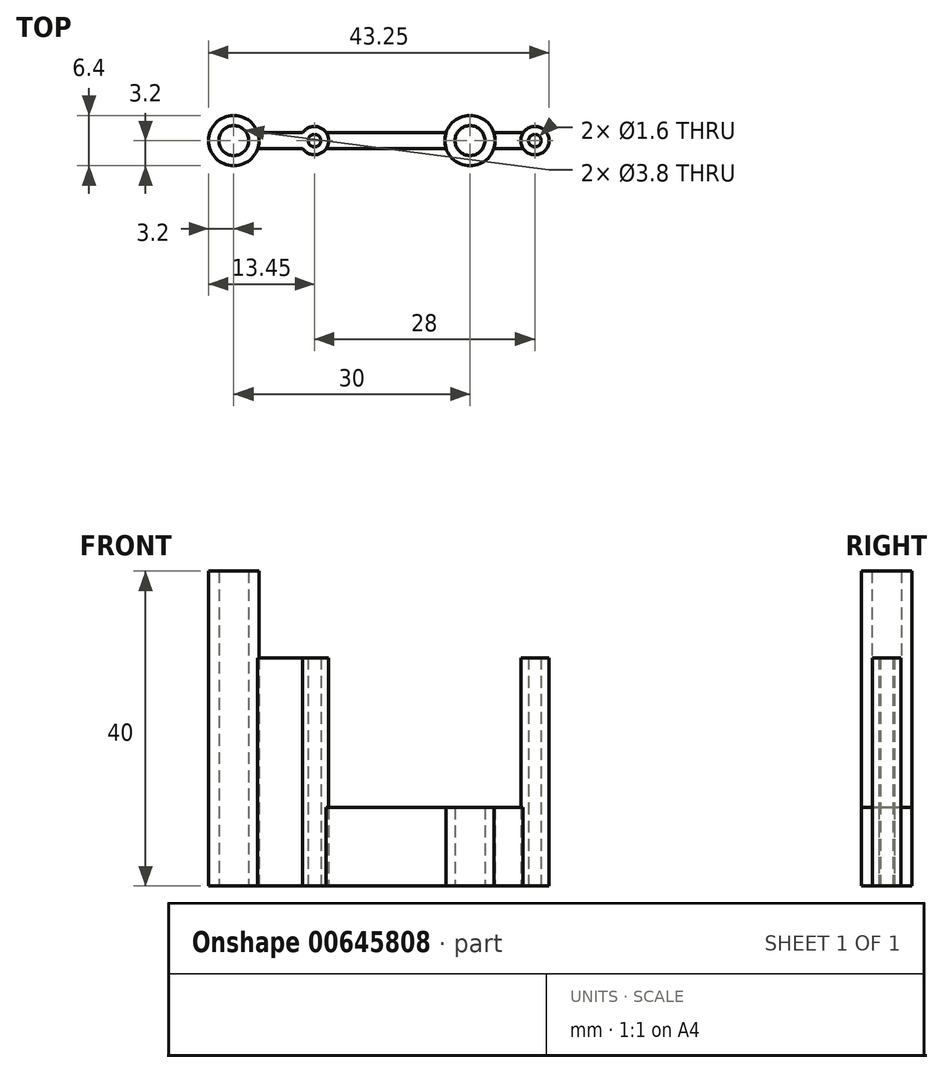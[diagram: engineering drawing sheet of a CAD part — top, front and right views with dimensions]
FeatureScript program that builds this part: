
annotation { "Feature Type Name" : "Feature", "Feature Type Description" : "" }
export const myFeature = defineFeature(function(context is Context, id is Id, definition is map)
    precondition{}
    {
        {
            var Q0;
            Q0=qCreatedBy(makeId("Top.planeOp"),FACE);
            var sketch = newSketch(context, id + "F0", { "sketchPlane" : qUnion([Q0])});
            skCircle(sketch, "E0", {"center": v(-30, 0) * mm, "radius": 3.2 * mm});
            skCircle(sketch, "E1", {"center": v(0, 0) * mm, "radius": 3.2 * mm});
            skCircle(sketch, "E2", {"center": v(-30, 0) * mm, "radius": 1.9 * mm});
            skCircle(sketch, "E3", {"center": v(0, 0) * mm, "radius": 1.9 * mm});
            skCircle(sketch, "E4", {"center": v(8.25, 0) * mm, "radius": 0.8 * mm});
            skCircle(sketch, "E5", {"center": v(8.25, 0) * mm, "radius": 1.8 * mm});
            skCircle(sketch, "E6", {"center": v(-19.75, 0) * mm, "radius": 0.8 * mm});
            skCircle(sketch, "E7", {"center": v(-19.75, 0) * mm, "radius": 1.8 * mm});
            skLineSegment(sketch, "E8", {"start": v(-26.96, 1) * mm, "end": v(-21.25, 1) * mm});
            skLineSegment(sketch, "E9", {"start": v(-26.96, -1) * mm, "end": v(-21.25, -1) * mm});
            skLineSegment(sketch, "E10", {"start": v(-18.25, 1) * mm, "end": v(-3.04, 1) * mm});
            skLineSegment(sketch, "E11", {"start": v(-18.25, -1) * mm, "end": v(-3.04, -1) * mm});
            skLineSegment(sketch, "E12", {"start": v(3.04, 1) * mm, "end": v(6.75, 1) * mm});
            skLineSegment(sketch, "E13", {"start": v(3.04, -1) * mm, "end": v(6.75, -1) * mm});
            skSolve(sketch);
        }
        {
            var Q0;
            Q0=makeQuery(id+"F0.imprint","IMPRINT",FACE,{"disambiguationData":[TD([[makeQuery(id+"F0.imprint","IMPRINT",EDGE,{"derivedFrom":sQuery(id+"F0.wireOp",EDGE,"E0")}),1.0]])]});
            extrude(context, id + "F1", {"entities" : qUnion([Q0]), "depth" : 40 * mm, "offsetDistance" : 25 * mm});
        }
        {
            var Q0;
            Q0=makeQuery(id+"F0.imprint","IMPRINT",FACE,{"disambiguationData":[TD([[makeQuery(id+"F0.imprint","IMPRINT",EDGE,{"derivedFrom":sQuery(id+"F0.wireOp",EDGE,"E1")}),1.0]])]});
            extrude(context, id + "F2", {"entities" : qUnion([Q0]), "operationType" : NewBodyOperationType.ADD, "depth" : 10 * mm, "offsetDistance" : 25 * mm});
        }
        {
            var Q0;
            Q0=makeQuery(id+"F0.imprint","IMPRINT",FACE,{"disambiguationData":[TD([[makeQuery(id+"F0.imprint","IMPRINT",EDGE,{"derivedFrom":sQuery(id+"F0.wireOp",EDGE,"E6")}),-1.0]])]});
            var Q1;
            Q1=makeQuery(id+"F0.imprint","IMPRINT",FACE,{"disambiguationData":[TD([[makeQuery(id+"F0.imprint","IMPRINT",EDGE,{"derivedFrom":sQuery(id+"F0.wireOp",EDGE,"E4")}),-1.0]])]});
            var Q2;
            {var subQ0=sQuery(id+"F0.wireOp",EDGE,"E8");Q2=makeQuery(id+"F0.imprint","IMPRINT",FACE,{"disambiguationData":[TD([[makeQuery(id+"F0.imprint","IMPRINT",EDGE,{"derivedFrom":subQ0}),-1.0]])]});}
            extrude(context, id + "F3", {"entities" : qUnion([Q0, Q1, Q2]), "depth" : 29 * mm, "offsetDistance" : 25 * mm});
        }
        {
            var Q0;
            {var subQ0=sQuery(id+"F0.wireOp",EDGE,"E10");Q0=makeQuery(id+"F0.imprint","IMPRINT",FACE,{"disambiguationData":[TD([[makeQuery(id+"F0.imprint","IMPRINT",EDGE,{"derivedFrom":subQ0}),-1.0]])]});}
            var Q1;
            {var subQ0=sQuery(id+"F0.wireOp",EDGE,"E12");Q1=makeQuery(id+"F0.imprint","IMPRINT",FACE,{"disambiguationData":[TD([[makeQuery(id+"F0.imprint","IMPRINT",EDGE,{"derivedFrom":subQ0}),-1.0]])]});}
            extrude(context, id + "F4", {"entities" : qUnion([Q0, Q1]), "depth" : 10 * mm, "offsetDistance" : 25 * mm});
        }
    });
